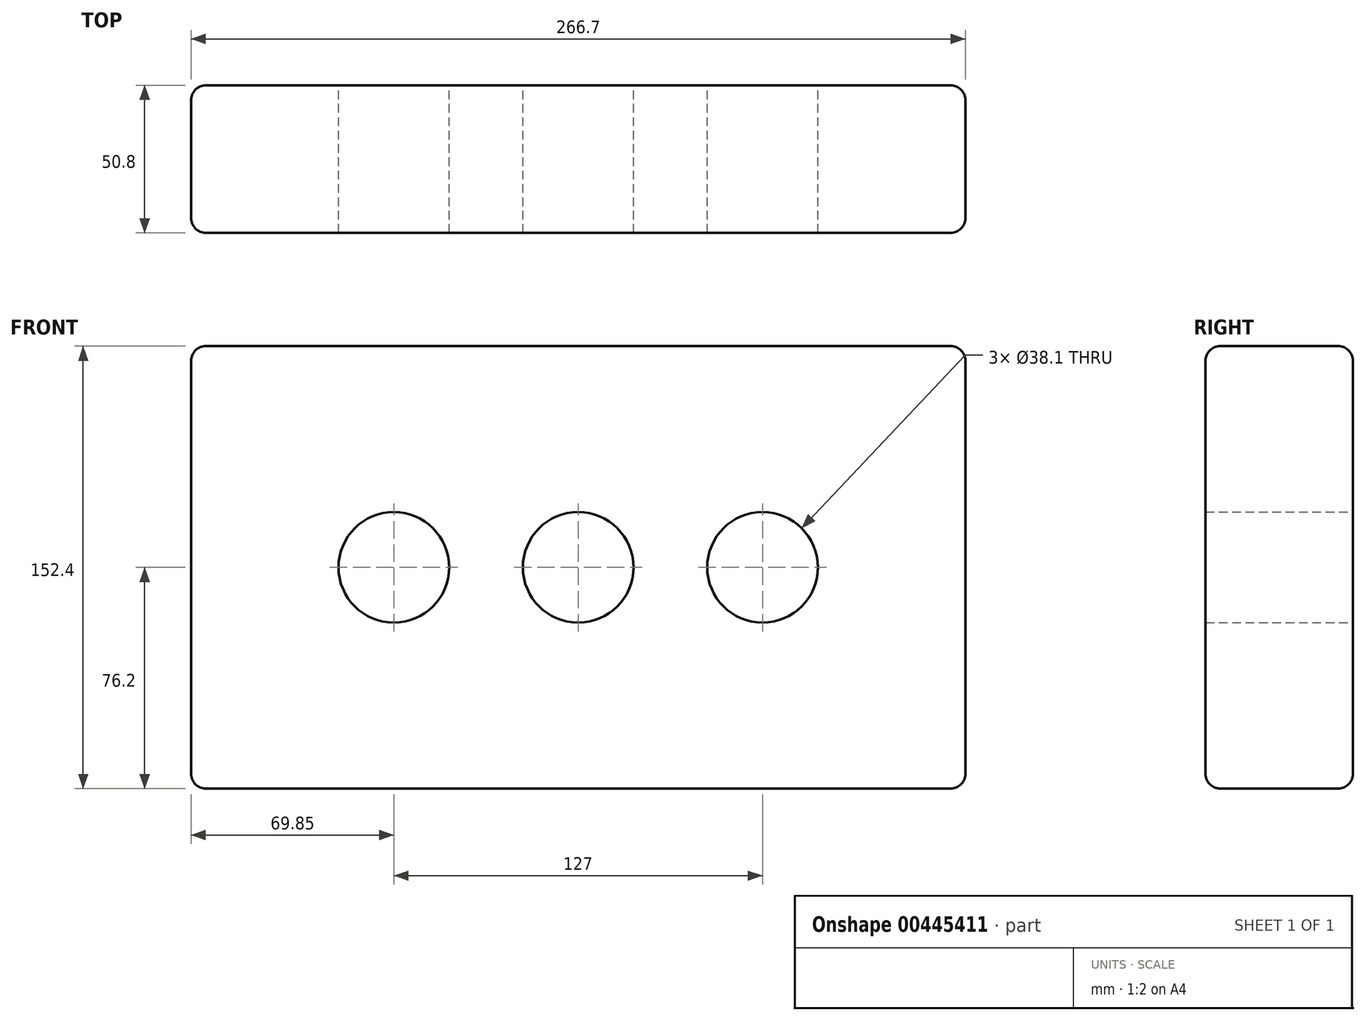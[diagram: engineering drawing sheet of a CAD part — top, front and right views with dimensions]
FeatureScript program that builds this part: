
annotation { "Feature Type Name" : "Feature", "Feature Type Description" : "" }
export const myFeature = defineFeature(function(context is Context, id is Id, definition is map)
    precondition{}
    {
        {
            var Q0;
            Q0=qCreatedBy(makeId("Front.planeOp"),FACE);
            var sketch = newSketch(context, id + "F0", { "sketchPlane" : qUnion([Q0])});
            skLineSegment(sketch, "E0.bottom", {"start": v(133.35, 76.2) * mm, "end": v(-133.35, 76.2) * mm});
            skLineSegment(sketch, "E0.top", {"start": v(133.35, -76.2) * mm, "end": v(-133.35, -76.2) * mm});
            skLineSegment(sketch, "E0.left", {"start": v(133.35, 76.2) * mm, "end": v(133.35, -76.2) * mm});
            skLineSegment(sketch, "E0.right", {"start": v(-133.35, 76.2) * mm, "end": v(-133.35, -76.2) * mm});
            skPoint(sketch, "E0.middle", {"position": v(0, 0) * mm});
            skCircle(sketch, "E1", {"center": v(0, 0) * mm, "radius": 19.05 * mm});
            skLineSegment(sketch, "E2", {"start": v(19.05, 0) * mm, "end": v(63.5, 0) * mm});
            skLineSegment(sketch, "E3", {"start": v(-19.05, 0) * mm, "end": v(-63.5, 0) * mm});
            skCircle(sketch, "E4", {"center": v(-63.5, 0) * mm, "radius": 19.05 * mm});
            skCircle(sketch, "E5", {"center": v(63.5, 0) * mm, "radius": 19.05 * mm});
            skSolve(sketch);
        }
        {
            var Q0;
            Q0 = qSketchRegion(id + "F0", true);
            var Q1;
            Q1=makeQuery(id+"F0.imprint","IMPRINT",FACE,{"disambiguationData":[TD([[makeQuery(id+"F0.imprint","IMPRINT",EDGE,{"derivedFrom":sQuery(id+"F0.wireOp",EDGE,"E0.bottom")}),1.0]])]});
            extrude(context, id + "F1", {"entities" : qUnion([Q0, Q1]), "depth" : 50.8 * mm});
        }
        {
            var Q0;
            Q0=makeQuery(id+"F1.opExtrude","SWEPT_FACE",FACE,{"disambiguationData":[OSD([sQuery(id+"F0.wireOp",EDGE,"E0.top")])]});
            var Q1;
            Q1=makeQuery(id+"F1.opExtrude","SWEPT_FACE",FACE,{"disambiguationData":[OSD([sQuery(id+"F0.wireOp",EDGE,"E0.bottom")])]});
            var Q2;
            Q2=makeQuery(id+"F1.opExtrude","SWEPT_FACE",FACE,{"disambiguationData":[OSD([sQuery(id+"F0.wireOp",EDGE,"E0.right")])]});
            var Q3;
            Q3=makeQuery(id+"F1.opExtrude","SWEPT_FACE",FACE,{"disambiguationData":[OSD([sQuery(id+"F0.wireOp",EDGE,"E0.left")])]});
            fillet(context, id + "F2", {"entities" : qUnion([Q0, Q1, Q2, Q3]), "radius" : 5.08 * mm, "tangentPropagation" : true, "allowEdgeOverflow" : false});
        }
    });
